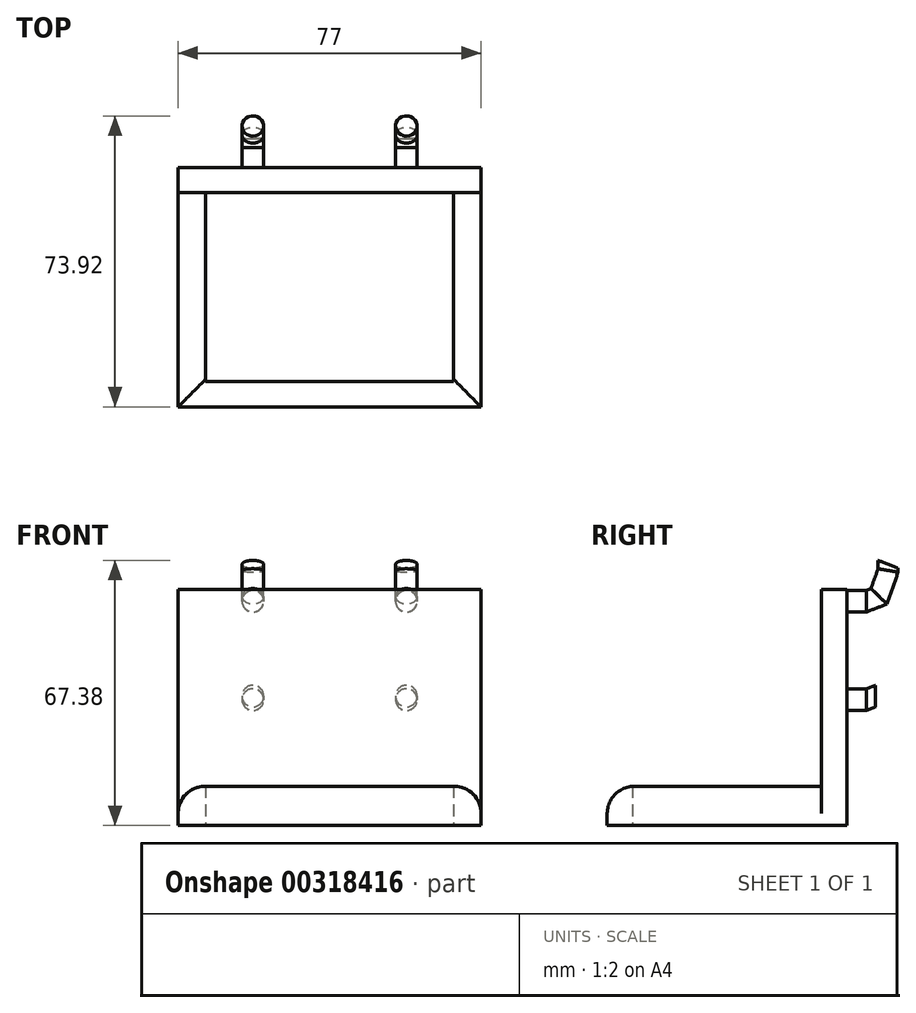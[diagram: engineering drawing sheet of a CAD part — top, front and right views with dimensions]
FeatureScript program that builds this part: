
annotation { "Feature Type Name" : "Feature", "Feature Type Description" : "" }
export const myFeature = defineFeature(function(context is Context, id is Id, definition is map)
    precondition{}
    {
        {
            var Q0;
            Q0=qCreatedBy(makeId("Top.planeOp"),FACE);
            var sketch = newSketch(context, id + "F0", { "sketchPlane" : qUnion([Q0])});
            skLineSegment(sketch, "E0.bottom", {"start": v(-38.5, 30.43) * mm, "end": v(38.5, 30.43) * mm});
            skLineSegment(sketch, "E0.top", {"start": v(-38.5, -30.43) * mm, "end": v(38.5, -30.43) * mm});
            skLineSegment(sketch, "E0.left", {"start": v(-38.5, 30.43) * mm, "end": v(-38.5, -30.43) * mm});
            skLineSegment(sketch, "E0.right", {"start": v(38.5, 30.43) * mm, "end": v(38.5, -30.43) * mm});
            skPoint(sketch, "E0.middle", {"position": v(0, 0) * mm});
            skLineSegment(sketch, "E1.bottom", {"start": v(31.5, 23.98) * mm, "end": v(-31.5, 23.98) * mm});
            skLineSegment(sketch, "E1.top", {"start": v(31.5, -23.98) * mm, "end": v(-31.5, -23.98) * mm});
            skLineSegment(sketch, "E1.left", {"start": v(31.5, 23.98) * mm, "end": v(31.5, -23.98) * mm});
            skLineSegment(sketch, "E1.right", {"start": v(-31.5, 23.98) * mm, "end": v(-31.5, -23.98) * mm});
            skSolve(sketch);
        }
        {
            var Q0;
            Q0=qSketchRegion(id+"F0",true);
            extrude(context, id + "F1", {"entities" : qUnion([Q0]), "depth" : 10 * mm});
        }
        {
            var Q0;
            Q0=makeQuery(id+"F1.opExtrude","CAP_FACE",FACE,{"disambiguationData":[OSD([sQuery(id+"F0.wireOp",EDGE,"E0.bottom"),sQuery(id+"F0.wireOp",EDGE,"E0.top"),sQuery(id+"F0.wireOp",EDGE,"E0.left"),sQuery(id+"F0.wireOp",EDGE,"E0.right"),sQuery(id+"F0.wireOp",EDGE,"E1.bottom"),sQuery(id+"F0.wireOp",EDGE,"E1.top"),sQuery(id+"F0.wireOp",EDGE,"E1.left"),sQuery(id+"F0.wireOp",EDGE,"E1.right")])],"isStart":false});
            var sketch = newSketch(context, id + "F2", { "sketchPlane" : qUnion([Q0])});
            skLineSegment(sketch, "E2.bottom", {"start": v(-38.5, 30.43) * mm, "end": v(38.5, 30.43) * mm});
            skLineSegment(sketch, "E2.top", {"start": v(-38.5, 23.98) * mm, "end": v(38.5, 23.98) * mm});
            skLineSegment(sketch, "E2.left", {"start": v(-38.5, 30.43) * mm, "end": v(-38.5, 23.98) * mm});
            skLineSegment(sketch, "E2.right", {"start": v(38.5, 30.43) * mm, "end": v(38.5, 23.98) * mm});
            skSolve(sketch);
        }
        {
            var Q0;
            Q0=qSketchRegion(id+"F2",true);
            extrude(context, id + "F3", {"entities" : qUnion([Q0]), "operationType" : NewBodyOperationType.ADD, "depth" : 50 * mm});
        }
        {
            var Q0;
            Q0=makeQuery(id+"F3.boolean.opBoolean","MERGE",FACE,{"derivedFrom":[makeQuery(id+"F1.opExtrude","SWEPT_FACE",FACE,{"disambiguationData":[OSD([sQuery(id+"F0.wireOp",EDGE,"E0.bottom")])]}),makeQuery(id+"F3.opExtrude","SWEPT_FACE",FACE,{"disambiguationData":[OSD([sQuery(id+"F2.wireOp",EDGE,"E2.bottom")])]})]});
            var sketch = newSketch(context, id + "F4", { "sketchPlane" : qUnion([Q0])});
            skCircle(sketch, "E3", {"center": v(-19.5, 57) * mm, "radius": 2.75 * mm});
            skCircle(sketch, "E4", {"center": v(-19.5, 32) * mm, "radius": 2.75 * mm});
            skCircle(sketch, "E5.MirrorC", {"center": v(19.5, 57) * mm, "radius": 2.75 * mm});
            skCircle(sketch, "E6.MirrorC", {"center": v(19.5, 32) * mm, "radius": 2.75 * mm});
            skSolve(sketch);
        }
        {
            var Q0;
            Q0=qSketchRegion(id+"F4",true);
            extrude(context, id + "F5", {"entities" : qUnion([Q0]), "operationType" : NewBodyOperationType.ADD, "depth" : 5 * mm});
        }
        {
            var Q0;
            Q0=qCreatedBy(makeId("Right.planeOp"),FACE);
            var sketch = newSketch(context, id + "F6", { "sketchPlane" : qUnion([Q0])});
            skLineSegment(sketch, "E7", {"start": v(35.4, 56.99) * mm, "end": v(38.64, 58.26) * mm});
            skLineSegment(sketch, "E8", {"start": v(38.64, 58.26) * mm, "end": v(40.94, 64.83) * mm});
            skLineSegment(sketch, "E9", {"start": v(40.94, 64.83) * mm, "end": v(40.94, 66.37) * mm});
            skLineSegment(sketch, "E10", {"start": v(35.39, 32.1) * mm, "end": v(37.78, 33) * mm});
            skSolve(sketch);
        }
        {
            var Q0;
            Q0=makeQuery(id+"F5.opExtrude","CAP_FACE",FACE,{"disambiguationData":[OSD([sQuery(id+"F4.wireOp",EDGE,"E3")])],"isStart":false});
            var Q1;
            Q1=makeQuery(id+"F5.opExtrude","CAP_FACE",FACE,{"disambiguationData":[OSD([sQuery(id+"F4.wireOp",EDGE,"E5.MirrorC")])],"isStart":false});
            var Q2;
            Q2=sQuery(id+"F6.wireOp",EDGE,"E7");
            var Q3;
            Q3=sQuery(id+"F6.wireOp",EDGE,"E8");
            var Q4;
            Q4=sQuery(id+"F6.wireOp",EDGE,"E9");
            sweep(context, id + "F7", {"operationType" : NewBodyOperationType.ADD, "profiles" : qUnion([Q0, Q1]), "path" : qUnion([Q2, Q3, Q4])});
        }
        {
            var Q0;
            Q0=makeQuery(id+"F5.opExtrude","CAP_FACE",FACE,{"disambiguationData":[OSD([sQuery(id+"F4.wireOp",EDGE,"E4")])],"isStart":false});
            var Q1;
            Q1=makeQuery(id+"F5.opExtrude","CAP_FACE",FACE,{"disambiguationData":[OSD([sQuery(id+"F4.wireOp",EDGE,"E6.MirrorC")])],"isStart":false});
            var Q2;
            Q2=qSketchRegion(id+"F6",true);
            var Q3;
            Q3=sQuery(id+"F6.wireOp",EDGE,"E10");
            sweep(context, id + "F8", {"operationType" : NewBodyOperationType.ADD, "profiles" : qUnion([Q0, Q1, Q2]), "path" : qUnion([Q3])});
        }
        {
            var Q0;
            Q0=makeQuery(id+"F1.opExtrude","CAP_EDGE",EDGE,{"disambiguationData":[OSD([sQuery(id+"F0.wireOp",EDGE,"E0.left")])],"isStart":false});
            var Q1;
            Q1=makeQuery(id+"F1.opExtrude","CAP_EDGE",EDGE,{"disambiguationData":[OSD([sQuery(id+"F0.wireOp",EDGE,"E0.right")])],"isStart":false});
            var Q2;
            Q2=makeQuery(id+"F1.opExtrude","CAP_EDGE",EDGE,{"disambiguationData":[OSD([sQuery(id+"F0.wireOp",EDGE,"E0.top")])],"isStart":false});
            fillet(context, id + "F9", {"entities" : qUnion([Q0, Q1, Q2]), "radius" : 6.9 * mm, "tangentPropagation" : true, "allowEdgeOverflow" : false});
        }
    });
